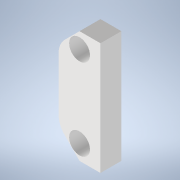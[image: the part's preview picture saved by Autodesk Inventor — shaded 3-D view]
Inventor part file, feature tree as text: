
AUTODESK INVENTOR PART (.ipt)
format: ipt  version: 2020 (Build 240168000, 168)  size: 224,768 bytes
history: native  units: mm
features: reference x11, sketch x9, extrude x8, other x3, projected_geometry x2, revolve x1, plane x1, mirror x1, chamfer x1
ambient origin geometry x8: Origin, YZ Plane, XZ Plane, XY Plane, X Axis, Y Axis, Z Axis, Center Point
bodies: Volumenkörper1 (feature_tree)
feature tree (37):
  extrude  "Extrusion1"  Depth=4.0mm
  extrude  "Extrusion2"  Depth=2.0mm TaperAngle=0.0deg
  revolve  "Umdrehung1"
  extrude  "Extrusion3"  Depth=3.0mm
  extrude  "Extrusion4"  Depth=1.0mm TaperAngle=0.0deg
  extrude  "Extrusion5"  Depth=1.0mm TaperAngle=0.0deg
  plane  "Arbeitsebene1"
  extrude  "Extrusion8"  Depth=5.0mm
  extrude  "Extrusion9"  TaperAngle=0.0deg  [1 undecoded]
  mirror  "Spiegeln3"
  extrude  "Extrusion10"  Depth=2.0mm TaperAngle=45.0deg
  chamfer  "Fase2"  [1 undecoded]
  sketch  "Skizze1"  dims[d0=4.0mm d1=0.0mm d2=2.1mm]
  reference  "Referenz1"
  reference  "Referenz2"
  reference  "Referenz3"
  reference  "Referenz4"
  reference  "Referenz5"
  reference  "Referenz6"
  reference  "Referenz7"
  reference  "Referenz8"
  reference  "Referenz9"
  reference  "Referenz10"
  reference  "Referenz11"
  sketch  "Skizze2"  dims[d3=2.1mm d4=2.0mm d5=0.0mm]
  projected_geometry  "Projizierte Kontur1"
  sketch  "Skizze3"  dims[d7=8.5mm d8=3.0mm]
  sketch  "Skizze4"  dims[d9=90.0deg d10=1.0mm d11=0.0mm]
  sketch  "Skizze5"  dims[d12=1.0mm d13=0.0mm d14=1.0mm d15=0.0mm]
  projected_geometry  "Projizierte Kontur2"
  sketch  "Skizze6"  dims[d16=-10.75mm d24=5.0mm]
  sketch  "Skizze9"  dims[d25=0.0mm d26=0.0mm d27=0.0mm d28=0.0mm]
  sketch  "Skizze10"  dims[d29=0.0mm d30=0.0mm d31=0.5mm d32=2.0mm d33=45.0deg]
  sketch  "Skizze11"
  parser-record x1  (decoder bookkeeping rows leaked as tree rows — omitted from the tree; the rows remain in map.json)
  other  "GlassesAssembly.iam"
  other  "CameraMold:1"
note: 2 required parameter values undecoded (feature->parameter linkage not recoverable at this tier; creation-order binding heuristic only, values carry confidence <= 0.55)
note: 1 file-system path scrubbed to <path> (originals preserved in map.json)
